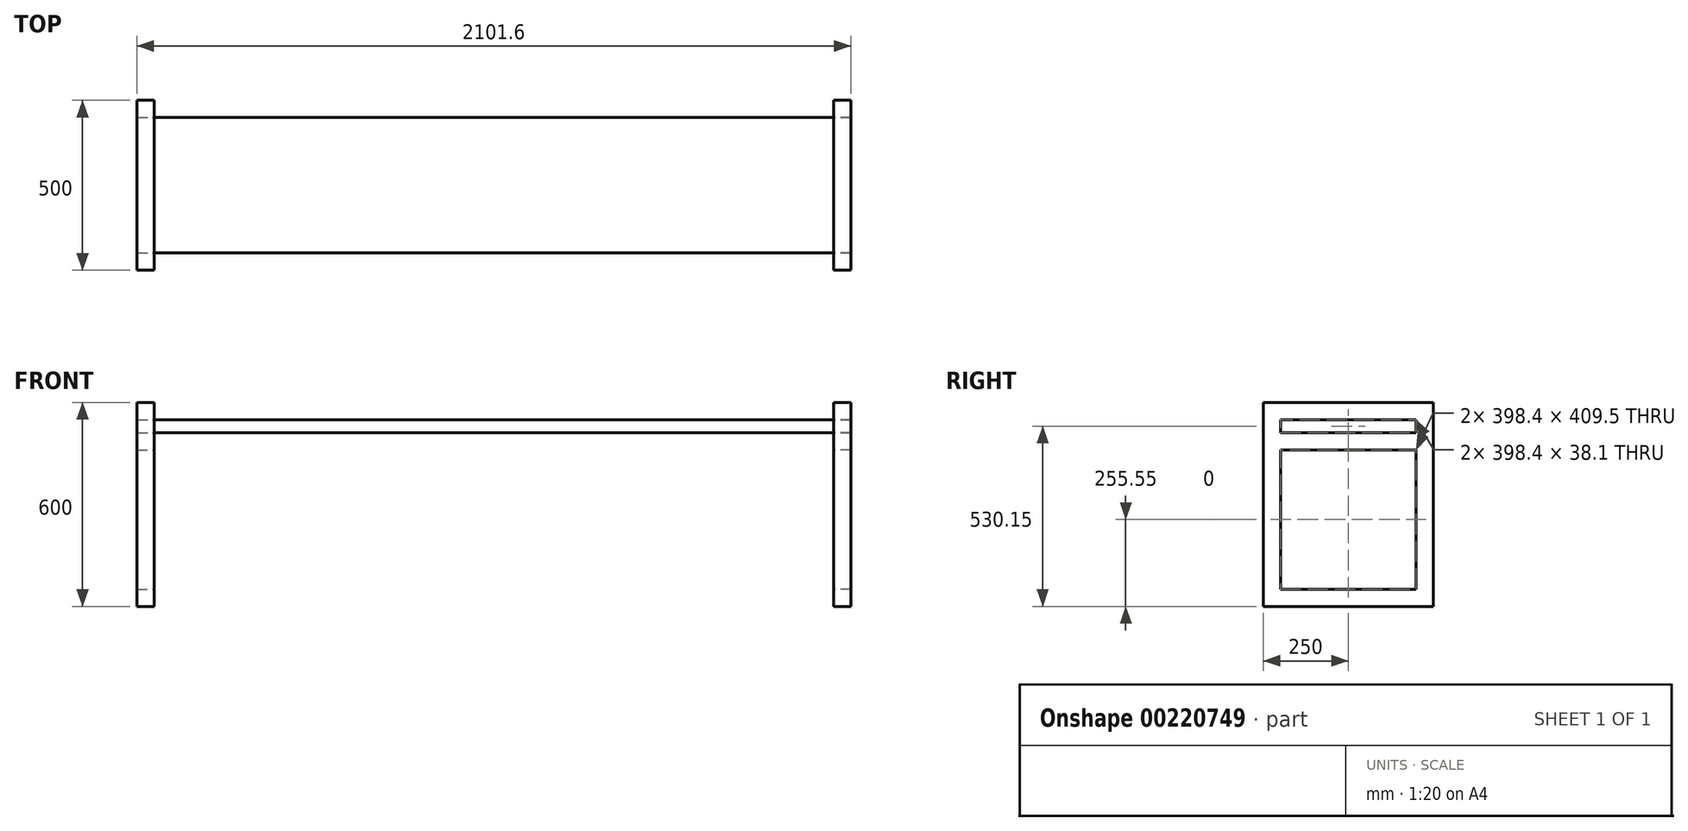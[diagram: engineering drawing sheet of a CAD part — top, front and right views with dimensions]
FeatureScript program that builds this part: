
annotation { "Feature Type Name" : "Feature", "Feature Type Description" : "" }
export const myFeature = defineFeature(function(context is Context, id is Id, definition is map)
    precondition{}
    {
        {
            var Q0;
            Q0=qCreatedBy(makeId("Right.planeOp"),FACE);
            cPlane(context, id + "F0", {"entities" : qUnion([Q0]), "cplaneType" : CPlaneType.OFFSET, "offset" : 1000 * mm, "width" : 150 * mm, "height" : 150 * mm});
        }
        {
            var Q0;
            Q0=qCreatedBy(id+"F0.planeOp",FACE);
            var sketch = newSketch(context, id + "F1", { "sketchPlane" : qUnion([Q0])});
            skLineSegment(sketch, "E0.bottom", {"start": v(0, 0) * mm, "end": v(-500, 0) * mm});
            skLineSegment(sketch, "E0.top", {"start": v(0, 600) * mm, "end": v(-500, 600) * mm});
            skLineSegment(sketch, "E0.left", {"start": v(0, 0) * mm, "end": v(0, 600) * mm});
            skLineSegment(sketch, "E0.right", {"start": v(-500, 0) * mm, "end": v(-500, 600) * mm});
            skLineSegment(sketch, "E1.0", {"start": v(-449.2, 50.8) * mm, "end": v(-449.2, 549.2) * mm});
            skLineSegment(sketch, "E1.1", {"start": v(-50.8, 50.8) * mm, "end": v(-449.2, 50.8) * mm});
            skLineSegment(sketch, "E1.2", {"start": v(-50.8, 50.8) * mm, "end": v(-50.8, 549.2) * mm});
            skLineSegment(sketch, "E1.3", {"start": v(-50.8, 549.2) * mm, "end": v(-449.2, 549.2) * mm});
            skSolve(sketch);
        }
        {
            var Q0;
            Q0 = qSketchRegion(id + "F1", true);
            extrude(context, id + "F2", {"entities" : qUnion([Q0]), "depth" : 50.8 * mm});
        }
        {
            var Q0;
            Q0=qCreatedBy(id+"F0.planeOp",FACE);
            var sketch = newSketch(context, id + "F3", { "sketchPlane" : qUnion([Q0])});
            skLineSegment(sketch, "E2.bottom", {"start": v(-449.2, 511.1) * mm, "end": v(-50.8, 511.1) * mm});
            skLineSegment(sketch, "E2.top", {"start": v(-449.2, 460.3) * mm, "end": v(-50.8, 460.3) * mm});
            skLineSegment(sketch, "E2.left", {"start": v(-449.2, 511.1) * mm, "end": v(-449.2, 460.3) * mm});
            skLineSegment(sketch, "E2.right", {"start": v(-50.8, 511.1) * mm, "end": v(-50.8, 460.3) * mm});
            skSolve(sketch);
        }
        {
            var Q0;
            Q0=makeQuery(id+"F3.imprint","IMPRINT",FACE,{"disambiguationData":[TD([[makeQuery(id+"F3.imprint","IMPRINT",EDGE,{"derivedFrom":sQuery(id+"F3.wireOp",EDGE,"E2.bottom")}),-1.0]])]});
            extrude(context, id + "F4", {"entities" : qUnion([Q0]), "operationType" : NewBodyOperationType.ADD, "depth" : 50.8 * mm});
        }
        {
            var Q0;
            Q0=makeQuery(id+"F2.opExtrude","SWEPT_BODY",BODY,{"disambiguationData":[OSD([sQuery(id+"F1.wireOp",EDGE,"E0.bottom"),sQuery(id+"F1.wireOp",EDGE,"E0.top"),sQuery(id+"F1.wireOp",EDGE,"E0.left"),sQuery(id+"F1.wireOp",EDGE,"E0.right"),sQuery(id+"F1.wireOp",EDGE,"E1.0"),sQuery(id+"F1.wireOp",EDGE,"E1.1"),sQuery(id+"F1.wireOp",EDGE,"E1.2"),sQuery(id+"F1.wireOp",EDGE,"E1.3")])]});
            var Q1;
            Q1=qCreatedBy(makeId("Right.planeOp"),FACE);
            mirror(context, id + "F5", {"entities" : qUnion([Q0]), "mirrorPlane" : qUnion([Q1])});
        }
        {
            var Q0;
            Q0=makeQuery(id+"F4.boolean.opBoolean","MERGE",FACE,{"derivedFrom":[makeQuery(id+"F2.opExtrude","CAP_FACE",FACE,{"disambiguationData":[OSD([sQuery(id+"F1.wireOp",EDGE,"E0.bottom"),sQuery(id+"F1.wireOp",EDGE,"E0.top"),sQuery(id+"F1.wireOp",EDGE,"E0.left"),sQuery(id+"F1.wireOp",EDGE,"E0.right"),sQuery(id+"F1.wireOp",EDGE,"E1.0"),sQuery(id+"F1.wireOp",EDGE,"E1.1"),sQuery(id+"F1.wireOp",EDGE,"E1.2"),sQuery(id+"F1.wireOp",EDGE,"E1.3")])],"isStart":false}),makeQuery(id+"F4.opExtrude","CAP_FACE",FACE,{"disambiguationData":[OSD([sQuery(id+"F3.wireOp",EDGE,"E2.bottom"),sQuery(id+"F3.wireOp",EDGE,"E2.top"),sQuery(id+"F3.wireOp",EDGE,"E2.left"),sQuery(id+"F3.wireOp",EDGE,"E2.right")])],"isStart":false})]});
            var sketch = newSketch(context, id + "F6", { "sketchPlane" : qUnion([Q0])});
            skLineSegment(sketch, "E3.bottom", {"start": v(-449.2, 549.2) * mm, "end": v(-50.8, 549.2) * mm});
            skLineSegment(sketch, "E3.top", {"start": v(-449.2, 511.1) * mm, "end": v(-50.8, 511.1) * mm});
            skLineSegment(sketch, "E3.left", {"start": v(-449.2, 549.2) * mm, "end": v(-449.2, 511.1) * mm});
            skLineSegment(sketch, "E3.right", {"start": v(-50.8, 549.2) * mm, "end": v(-50.8, 511.1) * mm});
            skSolve(sketch);
        }
        {
            var Q0;
            Q0=makeQuery(id+"F6.imprint","IMPRINT",FACE,{"disambiguationData":[TD([[makeQuery(id+"F6.imprint","IMPRINT",EDGE,{"derivedFrom":sQuery(id+"F6.wireOp",EDGE,"E3.bottom")}),1.0]])]});
            extrude(context, id + "F7", {"entities" : qUnion([Q0]), "oppositeDirection" : true, "depth" : 2100 * mm});
        }
    });
